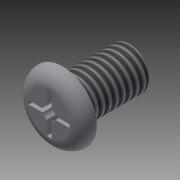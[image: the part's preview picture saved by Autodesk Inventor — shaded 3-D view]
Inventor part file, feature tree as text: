
AUTODESK INVENTOR PART (.ipt)
format: ipt  version: 2015 SP2 (Build 190223200, 223)  size: 154,624 bytes
history: native  units: mm
features: extrude x4, sketch x4, fillet x2, thread x1
ambient origin geometry x8: Origin, YZ Plane, XZ Plane, XY Plane, X Axis, Y Axis, Z Axis, Center Point
bodies: Solid1 (feature_tree)
feature tree (11):
  extrude  "Extrusion1"  Depth=5.0mm
  extrude  "Extrusion2"  Depth=1.0mm
  extrude  "Extrusion4"  Depth=1.0mm TaperAngle=0.0deg
  fillet  "Fillet1"  Radius=1.0mm
  fillet  "Fillet2"  Radius=1.0mm
  extrude  "Extrusion5"  Depth=0.1mm TaperAngle=0.0deg
  thread  "Thread1"  [1 undecoded]
  sketch  "Sketch1"  dims[d0=5.0mm d1=3.0mm]
  sketch  "Sketch2"  dims[d2=1.0mm d3=0.0mm d4=3.0mm]
  sketch  "Sketch4"  dims[d5=5.0mm d6=0.0mm d7=1.0mm d8=0.0mm d11=1.0mm d12=0.0mm d13=1.0mm]
  sketch  "Sketch5"  dims[d14=0.2mm d15=0.1mm d16=0.0mm d17=10.0mm d18=0.0mm]
note: 1 required parameter value undecoded (feature->parameter linkage not recoverable at this tier; creation-order binding heuristic only, values carry confidence <= 0.55)
